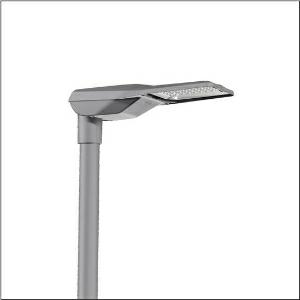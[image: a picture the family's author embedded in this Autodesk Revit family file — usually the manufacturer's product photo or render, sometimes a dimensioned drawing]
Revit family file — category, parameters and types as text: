
# Revit family: streetlight_sl_21_iq_mini___p0_5a_5xe2v31g08hb_63cb
name_source: partatom
category: Lighting Fixtures
units: mm (PartAtom-declared; Revit-internal decimal feet)

## family parameters
Cut with Voids When Loaded = No
Host = Face
Light Source = No
Part Type = Normal
Room Calculation Point = No
Round Connector Dimension = Use Diameter
Shared = No

## types (1)
- --- (1 x LED, 9290 lm, 70.9 W, 3000K)
    Apparent Load = 71 VA
    CIE Flux Codes = 37 73 96 100 100
    Color Rendering = 70
    Color Temperature = 3000K
    Default Elevation = 1800 mm
    Description = Streetlight SL 21 iQ mini, mast luminaire, primary light control with lens, of PMMA, primary optical cover: cover, of toughened safety glass, transparent, light distribution: P0.5a, light emission: direct distribution, primary light characteristic: asymmetric, installation type: post-top, side-entry, LED, High Power LED, rated luminous flux: 9.290lm, luminous efficacy: 131lm/W, light colour: 730, colour temperature: 3000K, control gear: iQ Street-Remote, control: pre-setting: linear dimming characteristic, Street-Remote, Auto-Match, Temp-Guard, Lumen-Switch, Night-Set, Smart-Wire, Light-Fading, Desk-Remote (wireless, voltage-free reading and setting of iQ features in the workshop via application-optimized NFC function/RFID function), optimised constant luminous flux control (CLO 2.0), mains connection: 220..240V, AC, 50/60Hz, start of lifetime: 71W, end of service life: 75W, reduction: 31W, luminaire housing, of diecast aluminium, powder-coated, SITECO metallic grey (DB 702S), corrosivity category C5 high according to DIN EN ISO 12944, please order mast flange separately, inclination adjustable: 0°, 5°, 10°, 15°, sealing non-destructively replaceable, multi-level sealing system, length: 628mm, width: 235mm, height: 110mm, mast flange for spigot size: 42mm (side-entry): 5XC10008XM4, 60/48mm (side-entry/post-top): 5XC10108XM2, 76/60mm (side-entry/post-top): 5XC10108XM1, mounting height: 4..8m, protection rating (complete): IP66, insulation class (complete): insulation class II (safety insulation), certification: CE, ENEC, ENEC+, VDE, impact resistance: IK10, permissible operating ambient temperature for outdoor applications: -40..+50°C, standard-compliant lighting for roads and squares, packaging unit: 1 piece

Light Distribution: P0.5a
    Height = 110 mm
    Lamp = 1 x LED
    Lamp Light Flux = 9290 lm
    Lamp Power = 70.9 W
    Lamp count = 1
    Length = 625 mm
    Luminous efficacy = 131 lm/W
    Manufacturer = Siteco
    ModVariant = No
    Model = 5XE2V31G08HB
    Number of Poles = 1
    OnlyDefault = Yes
    Power Factor = 1
    Product Name = Streetlight SL 21 iQ mini | P0.5a
    Product group = mast luminaire | pylon top
    ProductGroupID = 6100
    Protection Class = Protection class II
    Protection Degree = IP 66
    RLX_Detail_Level = 1
    RLX_Emergency_Light_Flux = 0 lm
    RLX_Emergency_Type = 0
    RLX_Emergency_Type_DB = No
    RlxData = <blob elided: 92689 chars, md5=6789ab33>
    Socket = socket
    Standby Power = 0 W
    System Light Flux = 9290 lm
    System Power = 71 W
    Type Comments = factory setting: luminous flux: 100 % | dim-lin: 254 | 711 mA
    Type Image = l_1003519.jpg
    URL = http://relux.com
    VarID = @adj_077433
    Voltage = 0 V
    Weight = 0.00 kg
    Width = 234 mm

## geometry (parser evidence)
native form markers: Blend x4, Sweep x10
no freeform markers — native parametric forms only
